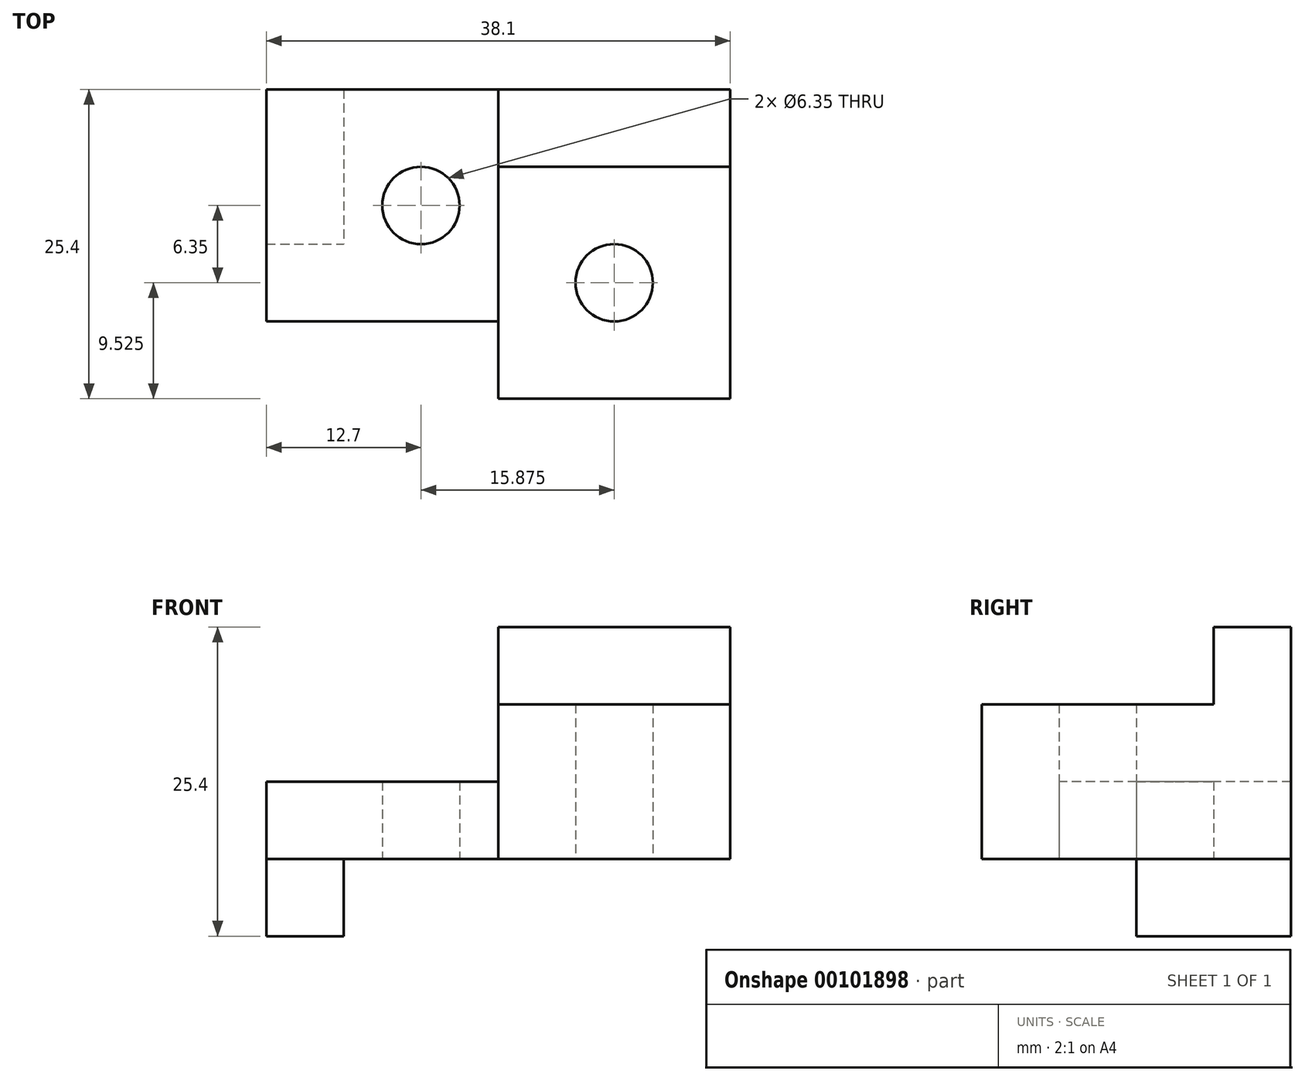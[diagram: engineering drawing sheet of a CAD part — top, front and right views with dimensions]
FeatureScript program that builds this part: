
annotation { "Feature Type Name" : "Feature", "Feature Type Description" : "" }
export const myFeature = defineFeature(function(context is Context, id is Id, definition is map)
    precondition{}
    {
        {
            var Q0;
            Q0=qCreatedBy(makeId("Top.planeOp"),FACE);
            var sketch = newSketch(context, id + "F0", { "sketchPlane" : qUnion([Q0])});
            skLineSegment(sketch, "E0.bottom", {"start": v(0, 0) * mm, "end": v(19.05, 0) * mm});
            skLineSegment(sketch, "E0.top", {"start": v(0, 19.05) * mm, "end": v(19.05, 19.05) * mm});
            skLineSegment(sketch, "E0.left", {"start": v(0, 0) * mm, "end": v(0, 19.05) * mm});
            skLineSegment(sketch, "E0.right", {"start": v(19.05, 0) * mm, "end": v(19.05, 19.05) * mm});
            skLineSegment(sketch, "E1.bottom", {"start": v(19.05, 19.05) * mm, "end": v(38.1, 19.05) * mm});
            skLineSegment(sketch, "E1.left", {"start": v(19.05, 19.05) * mm, "end": v(19.05, 12.7) * mm});
            skLineSegment(sketch, "E1.right", {"start": v(38.1, 19.05) * mm, "end": v(38.1, 12.7) * mm});
            skLineSegment(sketch, "E2.top", {"start": v(19.05, -6.35) * mm, "end": v(38.1, -6.35) * mm});
            skLineSegment(sketch, "E2.left", {"start": v(19.05, 12.7) * mm, "end": v(19.05, -6.35) * mm});
            skLineSegment(sketch, "E2.right", {"start": v(38.1, -6.35) * mm, "end": v(38.1, -6.35) * mm});
            skLineSegment(sketch, "E3", {"start": v(19.05, 12.7) * mm, "end": v(38.1, 12.7) * mm});
            skLineSegment(sketch, "E4", {"start": v(38.1, 12.7) * mm, "end": v(38.1, -6.35) * mm});
            skCircle(sketch, "E5", {"center": v(28.57, 3.18) * mm, "radius": 3.18 * mm});
            skCircle(sketch, "E6", {"center": v(12.7, 9.52) * mm, "radius": 3.18 * mm});
            skLineSegment(sketch, "E7", {"start": v(38.1, 12.7) * mm, "end": v(0, 12.7) * mm});
            skLineSegment(sketch, "E8", {"start": v(0, 12.7) * mm, "end": v(0, 0) * mm});
            skLineSegment(sketch, "E9", {"start": v(19.05, 0) * mm, "end": v(19.05, -6.35) * mm});
            skLineSegment(sketch, "E10", {"start": v(38.1, -6.35) * mm, "end": v(38.1, 12.7) * mm});
            skSolve(sketch);
        }
        {
            var Q0;
            Q0 = qSketchRegion(id + "F0", true);
            extrude(context, id + "F1", {"entities" : qUnion([Q0]), "depth" : 25.4 * mm});
        }
        {
            var Q0;
            Q0=qCreatedBy(makeId("Top.planeOp"),FACE);
            var sketch = newSketch(context, id + "F2", { "sketchPlane" : qUnion([Q0])});
            skLineSegment(sketch, "E11.bottom", {"start": v(6.35, 19.05) * mm, "end": v(38.1, 19.05) * mm});
            skLineSegment(sketch, "E11.left", {"start": v(6.35, 19.05) * mm, "end": v(6.35, 0) * mm});
            skLineSegment(sketch, "E11.right", {"start": v(38.1, 19.05) * mm, "end": v(38.1, -6.35) * mm});
            skLineSegment(sketch, "E12", {"start": v(6.35, 0) * mm, "end": v(19.05, 0) * mm});
            skLineSegment(sketch, "E13", {"start": v(19.05, 0) * mm, "end": v(19.05, -6.35) * mm});
            skLineSegment(sketch, "E14", {"start": v(19.05, -6.35) * mm, "end": v(38.1, -6.35) * mm});
            skSolve(sketch);
        }
        {
            var Q0;
            Q0 = qSketchRegion(id + "F2", true);
            extrude(context, id + "F3", {"entities" : qUnion([Q0]), "operationType" : NewBodyOperationType.REMOVE, "depth" : 6.35 * mm});
        }
        {
            var Q0;
            Q0=qCreatedBy(makeId("Front.planeOp"),FACE);
            var sketch = newSketch(context, id + "F4", { "sketchPlane" : qUnion([Q0])});
            skLineSegment(sketch, "E15.bottom", {"start": v(0, 0) * mm, "end": v(6.35, 0) * mm});
            skLineSegment(sketch, "E15.top", {"start": v(0, 6.35) * mm, "end": v(6.35, 6.35) * mm});
            skLineSegment(sketch, "E15.left", {"start": v(0, 0) * mm, "end": v(0, 6.35) * mm});
            skLineSegment(sketch, "E15.right", {"start": v(6.35, 0) * mm, "end": v(6.35, 6.35) * mm});
            skSolve(sketch);
        }
        {
            var Q0;
            Q0 = qSketchRegion(id + "F4", true);
            extrude(context, id + "F5", {"entities" : qUnion([Q0]), "operationType" : NewBodyOperationType.REMOVE, "oppositeDirection" : true, "depth" : 6.35 * mm});
        }
        {
            var Q0;
            Q0=qCreatedBy(makeId("Right.planeOp"),FACE);
            var sketch = newSketch(context, id + "F6", { "sketchPlane" : qUnion([Q0])});
            skLineSegment(sketch, "E16.bottom", {"start": v(-6.35, 25.4) * mm, "end": v(12.7, 25.4) * mm});
            skLineSegment(sketch, "E16.top", {"start": v(-6.35, 19.05) * mm, "end": v(12.7, 19.05) * mm});
            skLineSegment(sketch, "E16.left", {"start": v(-6.35, 25.4) * mm, "end": v(-6.35, 19.05) * mm});
            skLineSegment(sketch, "E16.right", {"start": v(12.7, 25.4) * mm, "end": v(12.7, 19.05) * mm});
            skSolve(sketch);
        }
        {
            var Q0;
            Q0 = qSketchRegion(id + "F6", true);
            extrude(context, id + "F7", {"entities" : qUnion([Q0]), "operationType" : NewBodyOperationType.REMOVE, "depth" : 38.1 * mm});
        }
        {
            var Q0;
            Q0=qCreatedBy(makeId("Front.planeOp"),FACE);
            var sketch = newSketch(context, id + "F8", { "sketchPlane" : qUnion([Q0])});
            skLineSegment(sketch, "E17.bottom", {"start": v(0, 25.4) * mm, "end": v(19.05, 25.4) * mm});
            skLineSegment(sketch, "E17.top", {"start": v(0, 12.7) * mm, "end": v(19.05, 12.7) * mm});
            skLineSegment(sketch, "E17.left", {"start": v(0, 25.4) * mm, "end": v(0, 12.7) * mm});
            skLineSegment(sketch, "E17.right", {"start": v(19.05, 25.4) * mm, "end": v(19.05, 12.7) * mm});
            skSolve(sketch);
        }
        {
            var Q0;
            Q0 = qSketchRegion(id + "F8", true);
            extrude(context, id + "F9", {"entities" : qUnion([Q0]), "operationType" : NewBodyOperationType.REMOVE, "oppositeDirection" : true, "depth" : 25.4 * mm});
        }
    });
